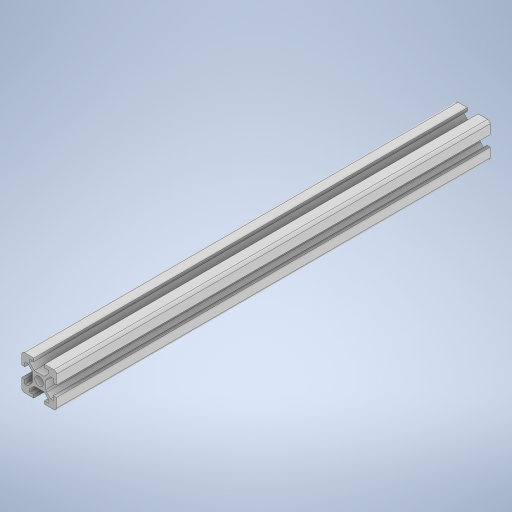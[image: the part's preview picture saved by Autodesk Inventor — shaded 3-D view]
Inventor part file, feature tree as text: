
AUTODESK INVENTOR PART (.ipt)
format: ipt  version: 2023.2 (Build 272271030, 271C)  size: 326,656 bytes
history: native  units: mm
features: extrude x1, fillet x1, sketch x1
ambient origin geometry x8: Origin, YZ Plane, XZ Plane, XY Plane, X Axis, Y Axis, Z Axis, Center Point
bodies: Solid1 (feature_tree)
feature tree (3):
  extrude  "Extrusion1"  Depth=20.0mm
  fillet  "Fillet1"  Radius=5.0mm
  sketch  "Sketch1"  dims[d8=20.0mm d9=20.0mm d10=5.0mm d18=6.1mm d19=6.1mm d21=1.5mm d24=4.5mm d25=4.5mm d26=1.5mm d27=6.9mm d28=1.8mm d29=250.0mm d30=0.0mm d31=1.5mm]
